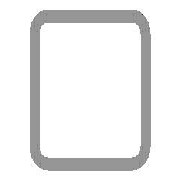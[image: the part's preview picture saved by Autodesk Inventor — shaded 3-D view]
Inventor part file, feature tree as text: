
AUTODESK INVENTOR PART (.ipt)
format: ipt  version: 2025 (Build 290162010, 162A)  size: 128,000 bytes
history: native  units: mm (DEFAULTED — no unit token found)
features: other x3, sketch x1, plane x1
ambient origin geometry x8: Origin, YZ Plane, XZ Plane, XY Plane, X Axis, Y Axis, Z Axis, Center Point
bodies: Solid1 (feature_tree), Body (feature_tree)
feature tree (5):
  other  "Driven Length"
  other  "Start plane"
  other  "End plane"
  sketch  "Sketch3"  dims[d3=2925.0mm d4=0.0mm d7=6.0mm d9=80.0mm d11=80.0mm d12=3.0mm d13=-0.0mm d14=2925.0mm d15=40.0mm d16=40.0mm d17=90.0deg d18=2925.0mm]
  plane  "Work Plane3"
